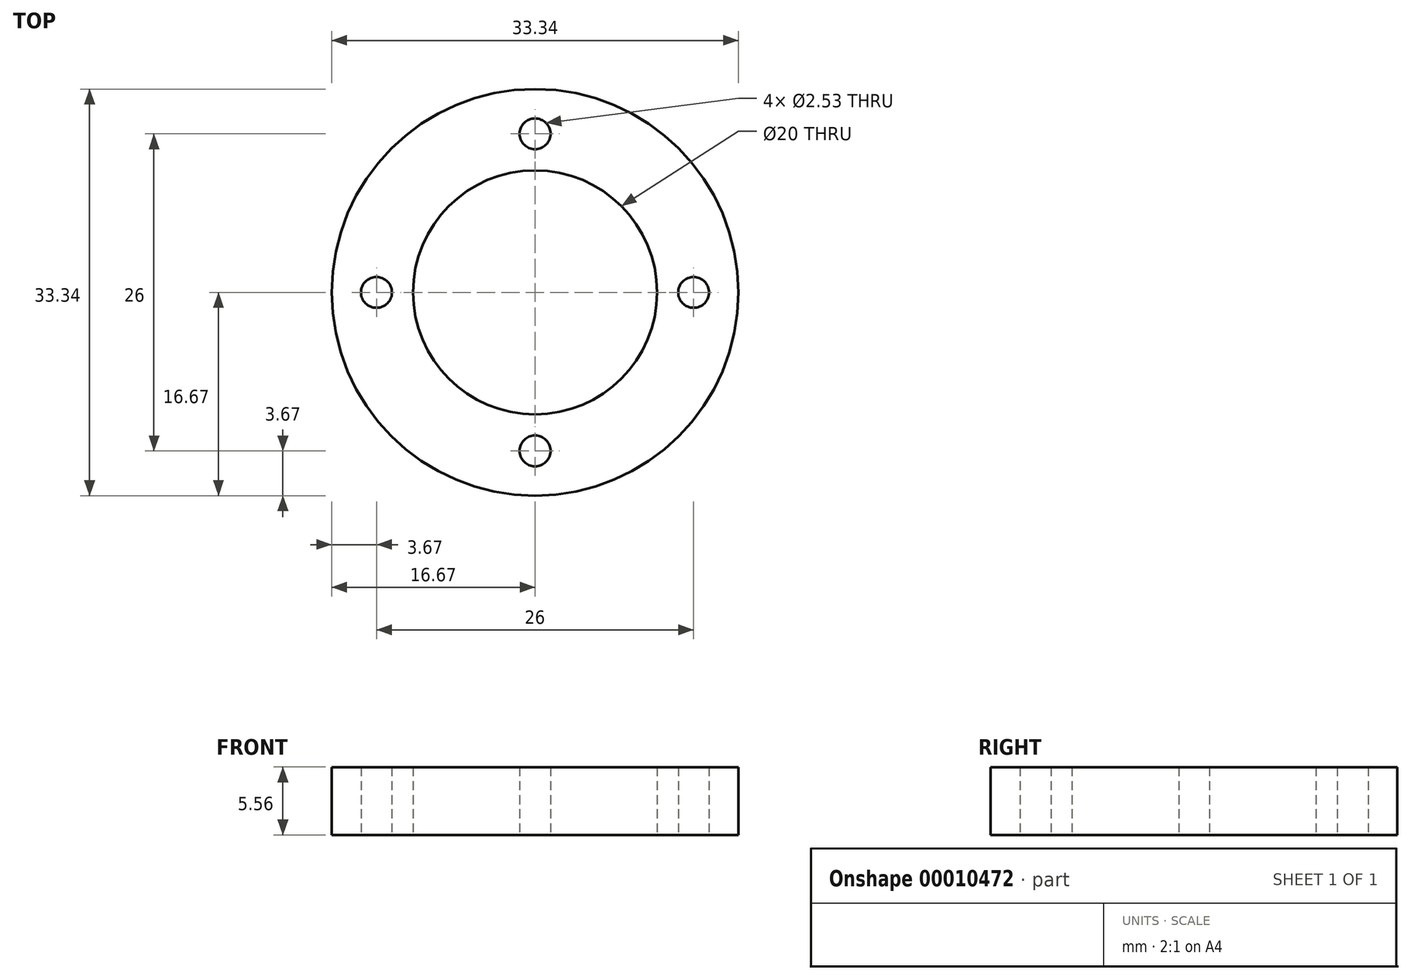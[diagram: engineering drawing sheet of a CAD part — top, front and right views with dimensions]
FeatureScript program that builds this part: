
annotation { "Feature Type Name" : "Feature", "Feature Type Description" : "" }
export const myFeature = defineFeature(function(context is Context, id is Id, definition is map)
    precondition{}
    {
        {
            var Q0;
            Q0=qCreatedBy(makeId("Top.planeOp"),FACE);
            var sketch = newSketch(context, id + "F0", { "sketchPlane" : qUnion([Q0])});
            skCircle(sketch, "E0", {"center": v(0, 0) * mm, "radius": 16.67 * mm});
            skCircle(sketch, "E1", {"center": v(0, 0) * mm, "radius": 10 * mm});
            skCircle(sketch, "E2", {"center": v(0, 0) * mm, "radius": 13 * mm, "construction": true});
            skCircle(sketch, "E3", {"center": v(-13, 0) * mm, "radius": 1.26 * mm});
            skCircle(sketch, "E4.1.0", {"center": v(0, -13) * mm, "radius": 1.26 * mm});
            skCircle(sketch, "E4.2.0", {"center": v(13, 0) * mm, "radius": 1.26 * mm});
            skCircle(sketch, "E4.3.0", {"center": v(0, 13) * mm, "radius": 1.26 * mm});
            skSolve(sketch);
        }
        {
            var Q0;
            Q0 = qSketchRegion(id + "F0", true);
            extrude(context, id + "F1", {"entities" : qUnion([Q0]), "depth" : 5.56 * mm});
        }
    });
